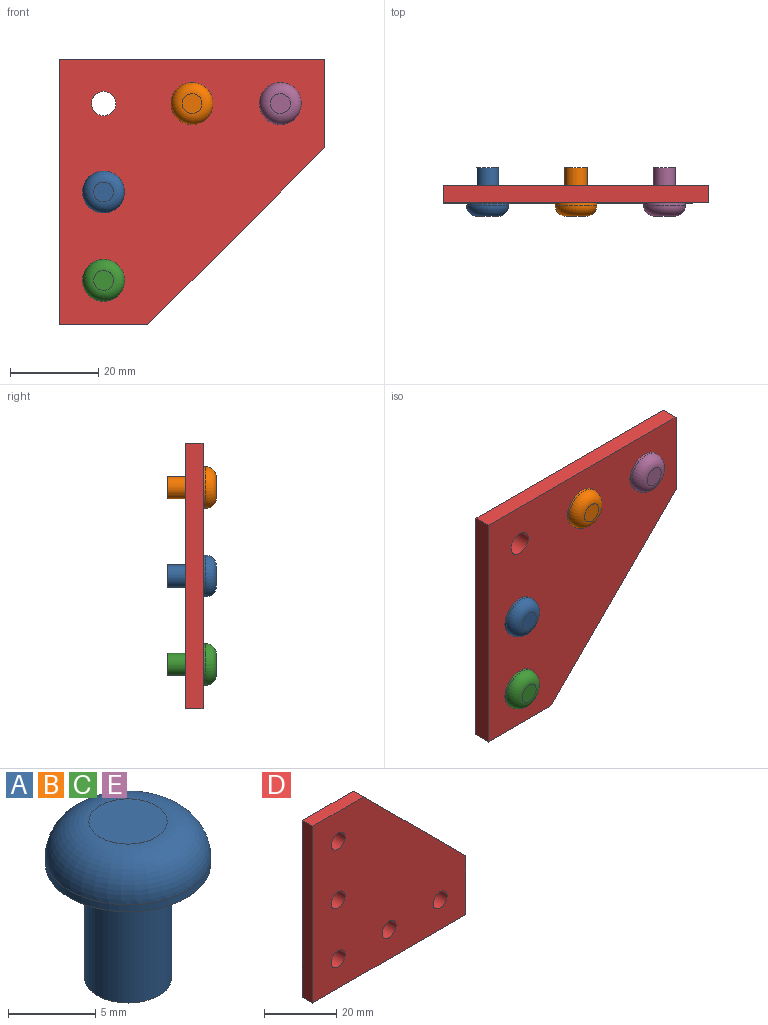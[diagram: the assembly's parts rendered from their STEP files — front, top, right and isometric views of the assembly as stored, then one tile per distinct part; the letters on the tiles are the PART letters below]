
ASSEMBLY  parts=5 mates=4
PART A: 6 faces, bbox 9.5x9.5x11 mm
  f0: cylinder r=4.75mm len=9.5mm, axis (0,0,-1), area 14.9mm2, adj f2,f3
  f1: plane 4.5x4.5mm, normal (0,0,1), area 15.9mm2, adj f3
  f2: plane 9.5x9.5mm, normal (0,0,-1), area 51.2mm2, adj f0,f4
  f3: torus R=2.25mm, axis (0,0,1), area 94.8mm2, adj f0,f1
  f4: cylinder r=2.5mm len=8mm, axis (0,0,1), area 125.7mm2, adj f2,f5
  f5: plane 5x5mm, normal (0,0,-1), area 19.6mm2, adj f4
PART B: same geometry as A
PART C: same geometry as A
PART D: 12 faces, bbox 60x4x60 mm
  f0: plane 40x40mm, normal (0.71,0,0.71), area 226.3mm2, adj f1,f9,f10,f11
  f1: plane 20x4mm, normal (0,0,1), area 80mm2, adj f0,f2,f10,f11
  f2: plane 60x4mm, normal (-1,0,0), area 240mm2, adj f1,f3,f10,f11
  f3: plane 60x4mm, normal (0,0,-1), area 240mm2, adj f2,f9,f10,f11
  f4: cylinder r=2.75mm len=5.5mm, axis (0,1,0), area 69.1mm2, adj f10,f11
  f5: cylinder r=2.75mm len=5.5mm, axis (0,1,0), area 69.1mm2, adj f10,f11
  f6: cylinder r=2.75mm len=5.5mm, axis (0,1,0), area 69.1mm2, adj f10,f11
  f7: cylinder r=2.75mm len=5.5mm, axis (0,1,0), area 69.1mm2, adj f10,f11
  f8: cylinder r=2.75mm len=5.5mm, axis (0,1,0), area 69.1mm2, adj f10,f11
  f9: plane 20x4mm, normal (1,0,0), area 80mm2, adj f0,f3,f10,f11
  f10: plane 60x60mm, normal (0,-1,0), area 2681.2mm2, adj f0,f1,f2,f3,f4,f5,f6,f7
  f11: plane 60x60mm, normal (0,1,0), area 2681.2mm2, adj f0,f1,f2,f3,f4,f5,f6,f7
PART E: same geometry as A
PLACE A rot(axis=(1,0,0),90deg) t=(-13.82,2.82,12.46)mm
PLACE B rot(axis=(1,0,0),90deg) t=(6.18,2.82,32.46)mm
PLACE C rot(axis=(1,0,0),90deg) t=(-13.82,2.82,-7.54)mm
PLACE D rot(axis=(0,1,0),90deg) t=(1.98,6.82,6.91)mm
PLACE E rot(axis=(1,0,0),90deg) t=(26.18,2.82,32.46)mm
MATE fastened B.f0 <-> D.f5  axis (0,-1,0) through (6.18,2.82,32.46)mm
MATE fastened D.f4 <-> E.f0  axis (0,-1,0) through (26.18,2.82,32.46)mm
MATE fastened D.f7 <-> A.f0  axis (0,-1,0) through (-13.82,2.82,12.46)mm
MATE fastened D.f8 <-> C.f0  axis (0,-1,0) through (-13.82,2.82,-7.54)mm
